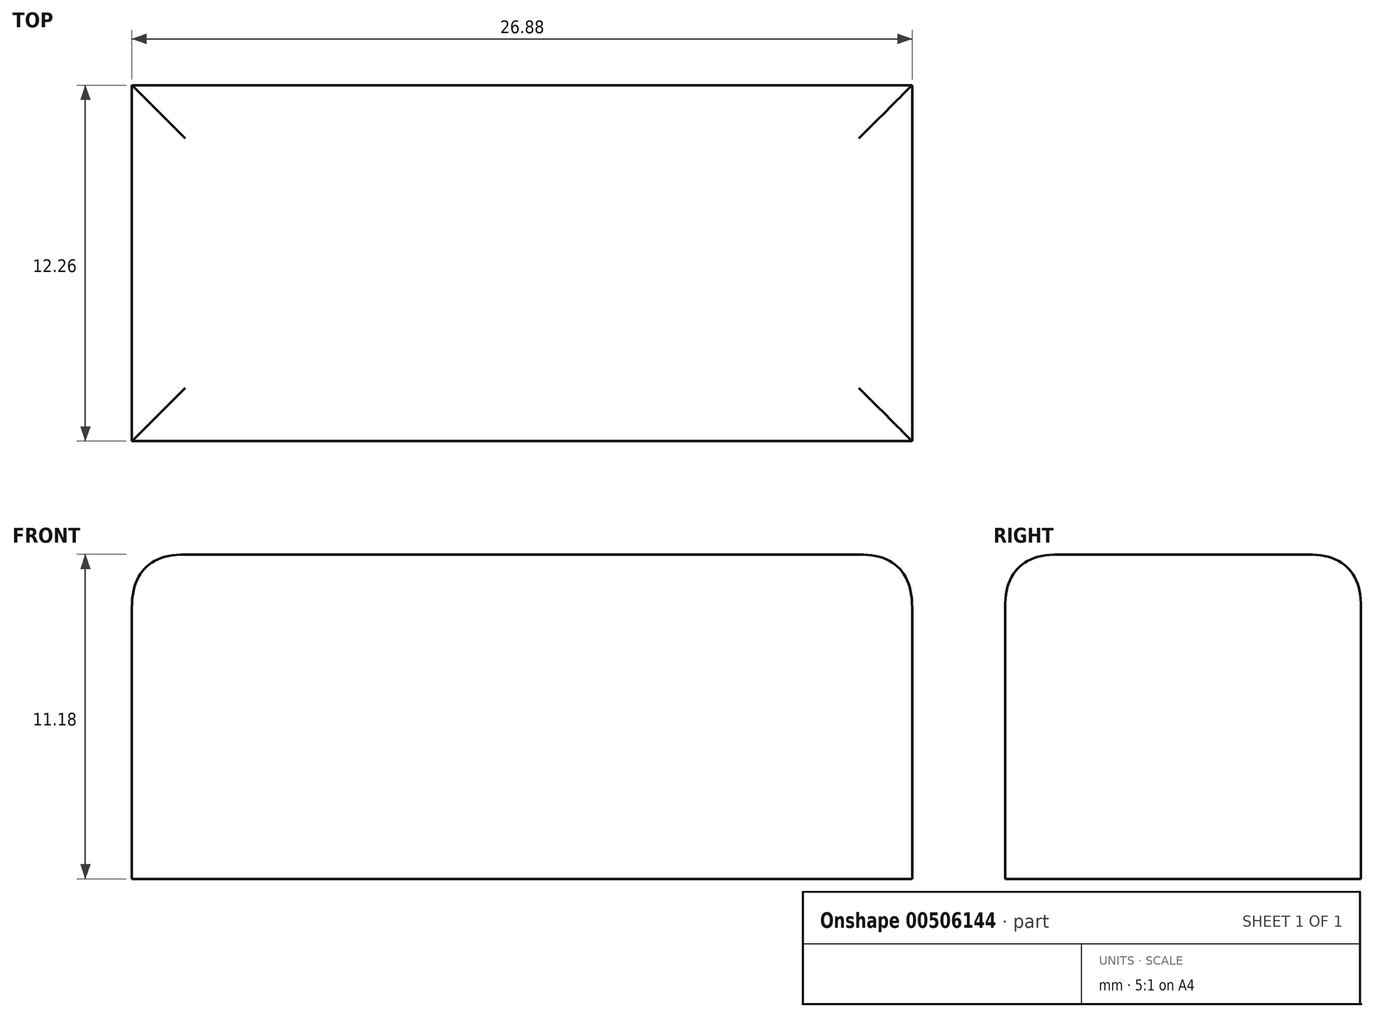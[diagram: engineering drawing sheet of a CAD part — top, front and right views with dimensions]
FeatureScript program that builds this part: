
annotation { "Feature Type Name" : "Feature", "Feature Type Description" : "" }
export const myFeature = defineFeature(function(context is Context, id is Id, definition is map)
    precondition{}
    {
        {
            var Q0;
            Q0=qCreatedBy(makeId("Top.planeOp"),FACE);
            var sketch = newSketch(context, id + "F0", { "sketchPlane" : qUnion([Q0])});
            skLineSegment(sketch, "E0.bottom", {"start": v(13.44, 6.13) * mm, "end": v(-13.44, 6.13) * mm});
            skLineSegment(sketch, "E0.top", {"start": v(13.44, -6.13) * mm, "end": v(-13.44, -6.13) * mm});
            skLineSegment(sketch, "E0.left", {"start": v(13.44, 6.13) * mm, "end": v(13.44, -6.13) * mm});
            skLineSegment(sketch, "E0.right", {"start": v(-13.44, 6.13) * mm, "end": v(-13.44, -6.13) * mm});
            skPoint(sketch, "E0.middle", {"position": v(0, 0) * mm});
            skSolve(sketch);
        }
        {
            var Q0;
            Q0 = qSketchRegion(id + "F0", true);
            extrude(context, id + "F1", {"entities" : qUnion([Q0]), "depth" : 11.18 * mm});
        }
        {
            var Q0;
            Q0=makeQuery(id+"F1.opExtrude","CAP_FACE",FACE,{"disambiguationData":[OSD([sQuery(id+"F0.wireOp",EDGE,"E0.bottom"),sQuery(id+"F0.wireOp",EDGE,"E0.top"),sQuery(id+"F0.wireOp",EDGE,"E0.left"),sQuery(id+"F0.wireOp",EDGE,"E0.right")])],"isStart":false});
            fillet(context, id + "F2", {"entities" : qUnion([Q0]), "radius" : 1.84 * mm, "tangentPropagation" : true, "rho" : 0.5, "crossSection" : FilletCrossSection.CONIC, "allowEdgeOverflow" : false});
        }
    });
